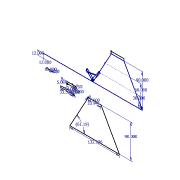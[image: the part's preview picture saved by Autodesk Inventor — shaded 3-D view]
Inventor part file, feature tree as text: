
AUTODESK INVENTOR PART (.ipt)
format: ipt  version: 2012 (Build 160160000, 160)  size: 97,280 bytes
history: native  units: in
note: dims shown in document units (in); Inventor stores cm internally (conversion verified against a paired STEP export)
features: sketch x1
ambient origin geometry x8: Origin, YZ Plane, XZ Plane, XY Plane, X Axis, Y Axis, Z Axis, Center Point
feature tree (1):
  sketch  "Sketch1"  dims[d6=30.0in d7=60.0in d9=90.0in d11=24.0in d12=5.0in d13=4.0in d14=132.9361in d15=33.9411in d16=90.0in d17=1.5in d18=1.25in d19=33.5in d20=4.0in d21=18.0in d22=4.0in d23=2.0in d24=12.0in d25=12.0in d26=0.4205in]
